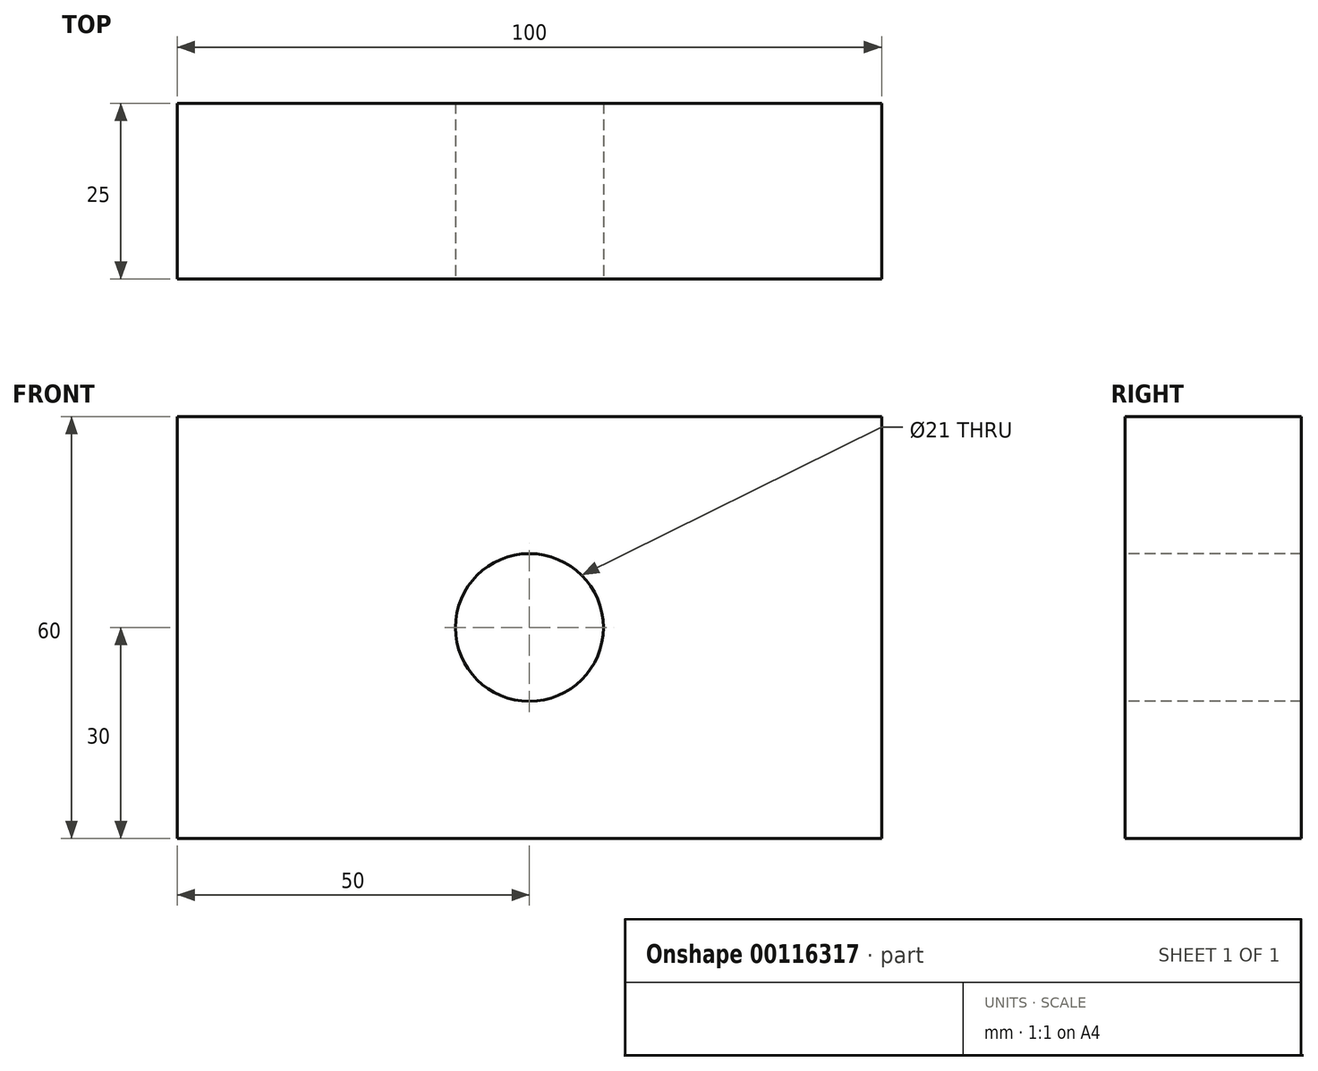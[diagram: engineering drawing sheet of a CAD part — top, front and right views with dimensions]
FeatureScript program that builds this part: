
annotation { "Feature Type Name" : "Feature", "Feature Type Description" : "" }
export const myFeature = defineFeature(function(context is Context, id is Id, definition is map)
    precondition{}
    {
        {
            var Q0;
            Q0=qCreatedBy(makeId("Front.planeOp"),FACE);
            var sketch = newSketch(context, id + "F0", { "sketchPlane" : qUnion([Q0])});
            skLineSegment(sketch, "E0.bottom", {"start": v(50, 30) * mm, "end": v(-50, 30) * mm});
            skLineSegment(sketch, "E0.top", {"start": v(50, -30) * mm, "end": v(-50, -30) * mm});
            skLineSegment(sketch, "E0.left", {"start": v(50, 30) * mm, "end": v(50, -30) * mm});
            skLineSegment(sketch, "E0.right", {"start": v(-50, 30) * mm, "end": v(-50, -30) * mm});
            skPoint(sketch, "E0.middle", {"position": v(0, 0) * mm});
            skSolve(sketch);
        }
        {
            var Q0;
            Q0=makeQuery(id+"F0.imprint","IMPRINT",FACE,{"disambiguationData":[TD([[makeQuery(id+"F0.imprint","IMPRINT",EDGE,{"derivedFrom":sQuery(id+"F0.wireOp",EDGE,"E0.bottom")}),1.0]])]});
            extrude(context, id + "F1", {"entities" : qUnion([Q0]), "endBound" : BoundingType.SYMMETRIC, "depth" : 25 * mm});
        }
        {
            var Q0;
            Q0=makeQuery(id+"F1.opExtrude","CAP_FACE",FACE,{"disambiguationData":[OSD([sQuery(id+"F0.wireOp",EDGE,"E0.bottom"),sQuery(id+"F0.wireOp",EDGE,"E0.top"),sQuery(id+"F0.wireOp",EDGE,"E0.left"),sQuery(id+"F0.wireOp",EDGE,"E0.right")])],"isStart":false});
            var sketch = newSketch(context, id + "F2", { "sketchPlane" : qUnion([Q0])});
            skCircle(sketch, "E1", {"center": v(0, 0) * mm, "radius": 10.5 * mm});
            skSolve(sketch);
        }
        {
            var Q0;
            Q0=makeQuery(id+"F2.imprint","IMPRINT",FACE,{"disambiguationData":[TD([[makeQuery(id+"F2.imprint","IMPRINT",EDGE,{"derivedFrom":sQuery(id+"F2.wireOp",EDGE,"E1")}),1.0]])]});
            extrude(context, id + "F3", {"entities" : qUnion([Q0]), "operationType" : NewBodyOperationType.REMOVE, "oppositeDirection" : true, "depth" : 25 * mm});
        }
    });
